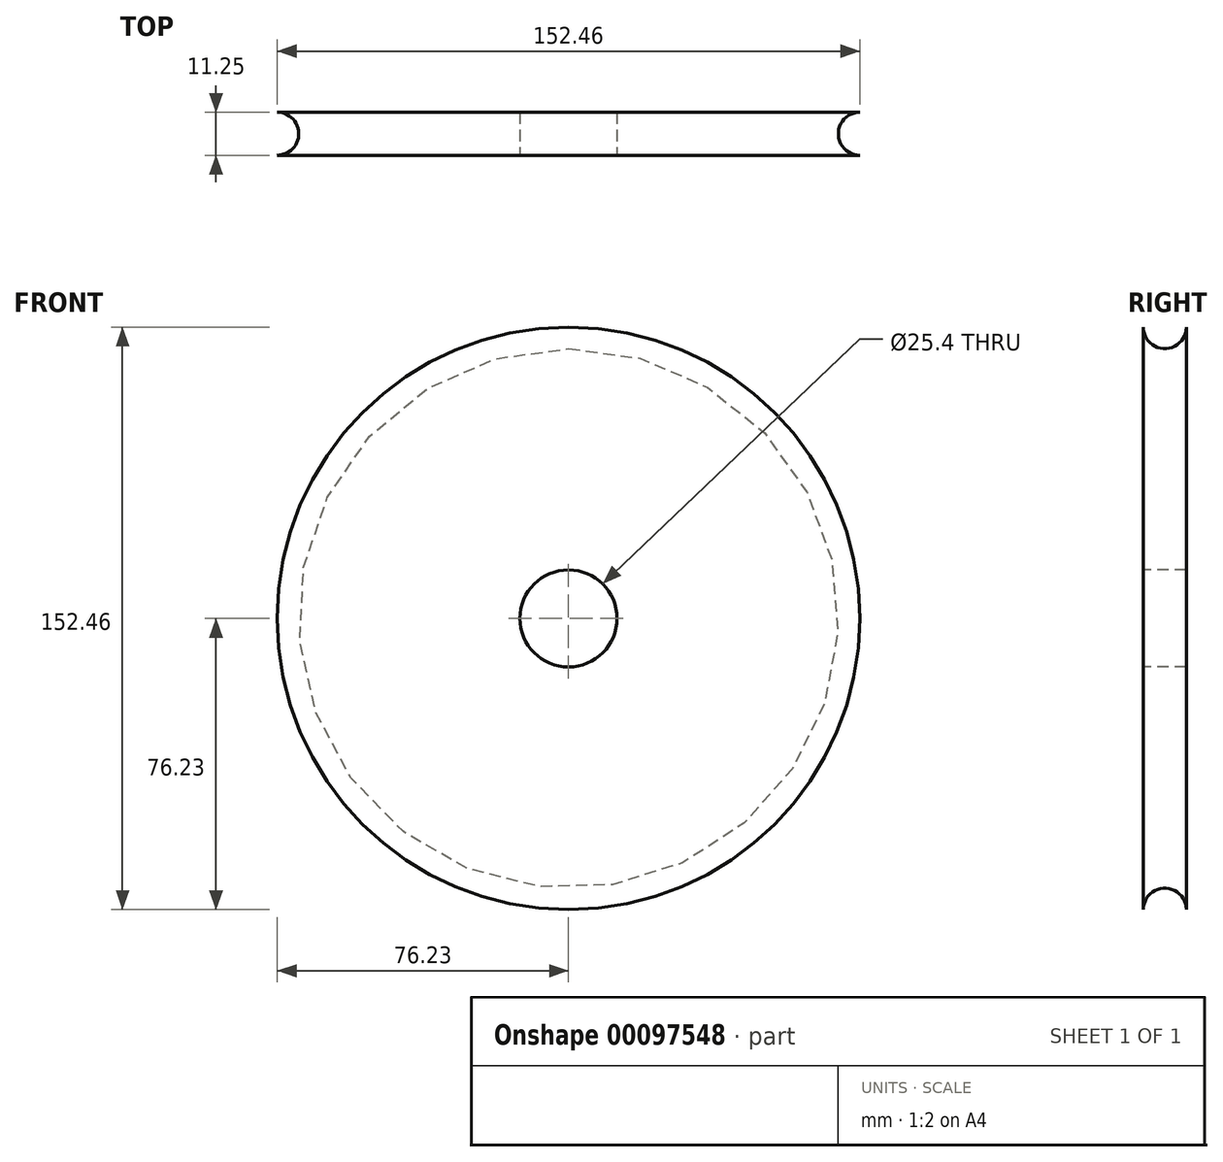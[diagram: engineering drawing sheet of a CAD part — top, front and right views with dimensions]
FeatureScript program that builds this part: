
annotation { "Feature Type Name" : "Feature", "Feature Type Description" : "" }
export const myFeature = defineFeature(function(context is Context, id is Id, definition is map)
    precondition{}
    {
        {
            var Q0;
            Q0=qCreatedBy(makeId("Top.planeOp"),FACE);
            var sketch = newSketch(context, id + "F0", { "sketchPlane" : qUnion([Q0])});
            skLineSegment(sketch, "E0.bottom", {"start": v(0, 0) * mm, "end": v(76.23, 0) * mm});
            skLineSegment(sketch, "E0.top", {"start": v(0, -11.25) * mm, "end": v(76.23, -11.25) * mm});
            skLineSegment(sketch, "E0.left", {"start": v(0, 0) * mm, "end": v(0, -11.25) * mm});
            skLineSegment(sketch, "E0.right", {"start": v(76.23, 0) * mm, "end": v(76.23, -11.25) * mm});
            skCircle(sketch, "E1", {"center": v(76.23, -5.62) * mm, "radius": 5.62 * mm});
            skSolve(sketch);
        }
        {
            var Q0;
            {var subQ0=sQuery(id+"F0.wireOp",EDGE,"E0.bottom");Q0=makeQuery(id+"F0.imprint","IMPRINT",FACE,{"disambiguationData":[TD([[makeQuery(id+"F0.imprint","IMPRINT",EDGE,{"derivedFrom":subQ0}),-1.0]])]});}
            var Q1;
            Q1=sQuery(id+"F0.wireOp",EDGE,"E0.left");
            revolve(context, id + "F1", {"entities" : qUnion([Q0]), "axis" : qUnion([Q1]), "revolveType" : RevolveType.FULL});
        }
        {
            var Q0;
            Q0=makeQuery(id+"F1.opRevolve","SWEPT_FACE",FACE,{"disambiguationData":[OSD([sQuery(id+"F0.wireOp",EDGE,"E0.top")])]});
            var sketch = newSketch(context, id + "F2", { "sketchPlane" : qUnion([Q0])});
            skCircle(sketch, "E2", {"center": v(0, 0) * mm, "radius": 12.7 * mm});
            skSolve(sketch);
        }
        {
            var Q0;
            Q0 = qSketchRegion(id + "F2", true);
            extrude(context, id + "F3", {"entities" : qUnion([Q0]), "operationType" : NewBodyOperationType.REMOVE, "oppositeDirection" : true, "depth" : 254 * mm});
        }
    });
